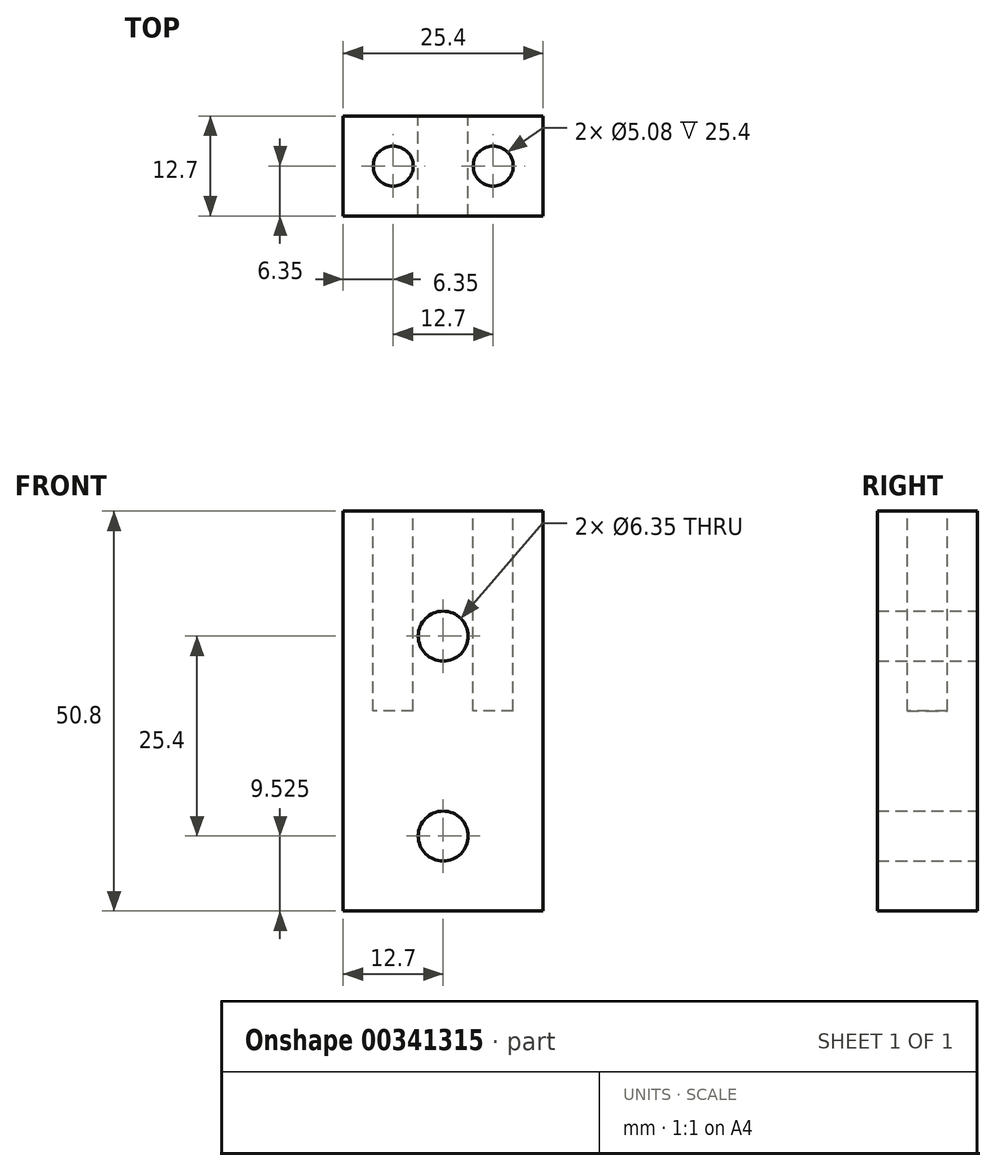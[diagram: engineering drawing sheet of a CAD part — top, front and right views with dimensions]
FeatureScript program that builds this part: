
annotation { "Feature Type Name" : "Feature", "Feature Type Description" : "" }
export const myFeature = defineFeature(function(context is Context, id is Id, definition is map)
    precondition{}
    {
        {
            var Q0;
            Q0=qCreatedBy(makeId("Front.planeOp"),FACE);
            var sketch = newSketch(context, id + "F0", { "sketchPlane" : qUnion([Q0])});
            skLineSegment(sketch, "E0.bottom", {"start": v(12.7, 25.4) * mm, "end": v(-12.7, 25.4) * mm});
            skLineSegment(sketch, "E0.top", {"start": v(12.7, -25.4) * mm, "end": v(-12.7, -25.4) * mm});
            skLineSegment(sketch, "E0.left", {"start": v(12.7, 25.4) * mm, "end": v(12.7, -25.4) * mm});
            skLineSegment(sketch, "E0.right", {"start": v(-12.7, 25.4) * mm, "end": v(-12.7, -25.4) * mm});
            skPoint(sketch, "E0.middle", {"position": v(0, 0) * mm});
            skCircle(sketch, "E1", {"center": v(0, 9.53) * mm, "radius": 3.18 * mm});
            skCircle(sketch, "E2", {"center": v(0, -15.88) * mm, "radius": 3.18 * mm});
            skSolve(sketch);
        }
        {
            var Q0;
            Q0 = qSketchRegion(id + "F0", true);
            extrude(context, id + "F1", {"entities" : qUnion([Q0]), "depth" : 12.7 * mm});
        }
        {
            var Q0;
            Q0=makeQuery(id+"F1.opExtrude","SWEPT_FACE",FACE,{"disambiguationData":[OSD([sQuery(id+"F0.wireOp",EDGE,"E0.bottom")])]});
            var sketch = newSketch(context, id + "F2", { "sketchPlane" : qUnion([Q0])});
            skCircle(sketch, "E3", {"center": v(-6.35, -6.35) * mm, "radius": 2.54 * mm});
            skCircle(sketch, "E4", {"center": v(6.35, -6.35) * mm, "radius": 2.54 * mm});
            skSolve(sketch);
        }
        {
            var Q0;
            Q0 = qSketchRegion(id + "F2", true);
            extrude(context, id + "F3", {"entities" : qUnion([Q0]), "operationType" : NewBodyOperationType.REMOVE, "oppositeDirection" : true, "depth" : 25.4 * mm});
        }
    });
